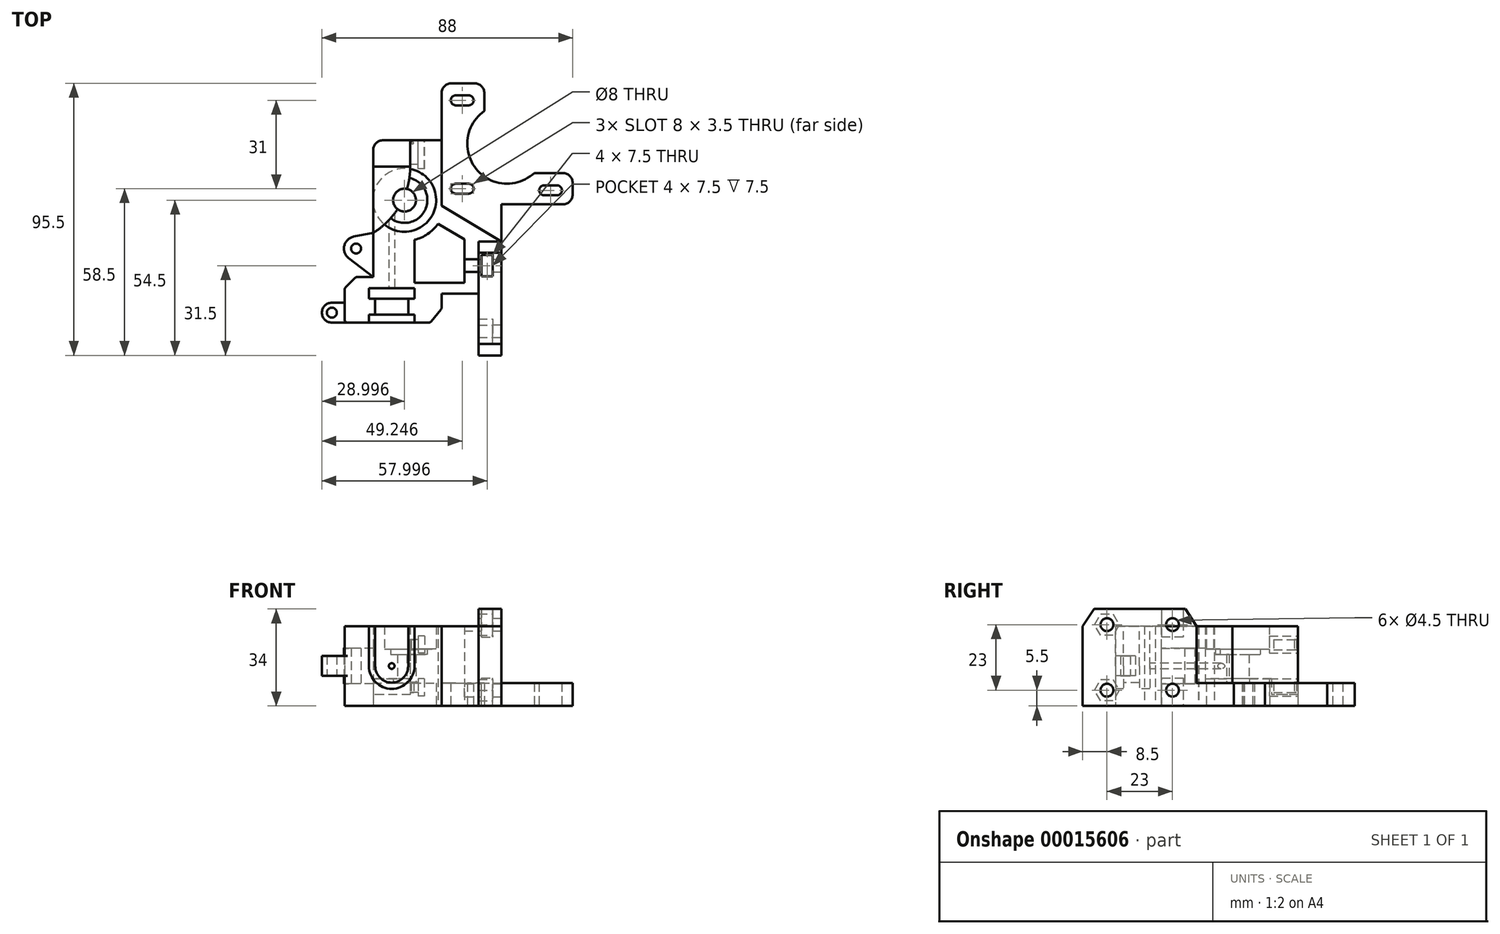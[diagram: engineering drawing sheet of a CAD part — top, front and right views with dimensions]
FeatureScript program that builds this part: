
annotation { "Feature Type Name" : "Feature", "Feature Type Description" : "" }
export const myFeature = defineFeature(function(context is Context, id is Id, definition is map)
    precondition{}
    {
        {
            var Q0;
            Q0=qCreatedBy(makeId("Top.planeOp"),FACE);
            var sketch = newSketch(context, id + "F0", { "sketchPlane" : qUnion([Q0])});
            skLineSegment(sketch, "E0.left", {"start": v(8.19, 39) * mm, "end": v(8.19, 0) * mm});
            skLineSegment(sketch, "E1", {"start": v(13.19, 7.25) * mm, "end": v(17.69, 7.25) * mm});
            skArc(sketch, "E2", {"start": v(13.19, 7.25) * mm, "mid": v(11.44, 5.5) * mm, "end": v(13.19, 3.75) * mm});
            skLineSegment(sketch, "E3", {"start": v(17.69, 3.75) * mm, "end": v(13.19, 3.75) * mm});
            skArc(sketch, "E4", {"start": v(17.69, 3.75) * mm, "mid": v(19.44, 5.5) * mm, "end": v(17.69, 7.25) * mm});
            skLineSegment(sketch, "E5", {"start": v(11.69, 42.5) * mm, "end": v(19.69, 42.5) * mm});
            skLineSegment(sketch, "E6", {"start": v(23.19, 39) * mm, "end": v(23.19, 32.76) * mm});
            skLineSegment(sketch, "E7", {"start": v(54.19, 3.5) * mm, "end": v(54.19, 7.5) * mm});
            skLineSegment(sketch, "E8", {"start": v(50.69, 11) * mm, "end": v(40.7, 11) * mm});
            skArc(sketch, "E9", {"start": v(23.19, 32.76) * mm, "mid": v(20.28, 12.5) * mm, "end": v(40.7, 11) * mm});
            skPoint(sketch, "E10.visualSharp", {"position": v(8.19, 42.5) * mm});
            skArc(sketch, "E10.filletArc", {"start": v(11.69, 42.5) * mm, "mid": v(9.21, 41.47) * mm, "end": v(8.19, 39) * mm});
            skPoint(sketch, "E11.visualSharp", {"position": v(23.19, 42.5) * mm});
            skArc(sketch, "E11.filletArc", {"start": v(23.19, 39) * mm, "mid": v(22.16, 41.47) * mm, "end": v(19.69, 42.5) * mm});
            skPoint(sketch, "E12.visualSharp", {"position": v(54.19, 11) * mm});
            skArc(sketch, "E12.filletArc", {"start": v(54.19, 7.5) * mm, "mid": v(53.16, 9.97) * mm, "end": v(50.69, 11) * mm});
            skPoint(sketch, "E13.visualSharp", {"position": v(54.19, 0) * mm});
            skArc(sketch, "E13.filletArc", {"start": v(50.69, 0) * mm, "mid": v(53.16, 1.03) * mm, "end": v(54.19, 3.5) * mm});
            skLineSegment(sketch, "E14", {"start": v(13.19, 38.25) * mm, "end": v(17.69, 38.25) * mm});
            skArc(sketch, "E15", {"start": v(17.69, 34.75) * mm, "mid": v(19.44, 36.5) * mm, "end": v(17.69, 38.25) * mm});
            skLineSegment(sketch, "E16", {"start": v(17.69, 34.75) * mm, "end": v(13.19, 34.75) * mm});
            skArc(sketch, "E17", {"start": v(13.19, 38.25) * mm, "mid": v(11.44, 36.5) * mm, "end": v(13.19, 34.75) * mm});
            skLineSegment(sketch, "E18", {"start": v(48.69, 3.18) * mm, "end": v(44.19, 3.18) * mm});
            skArc(sketch, "E19", {"start": v(44.19, 6.68) * mm, "mid": v(42.44, 4.93) * mm, "end": v(44.19, 3.18) * mm});
            skLineSegment(sketch, "E20", {"start": v(44.19, 6.68) * mm, "end": v(48.69, 6.68) * mm});
            skArc(sketch, "E21", {"start": v(48.69, 3.18) * mm, "mid": v(50.44, 4.93) * mm, "end": v(48.69, 6.68) * mm});
            skPoint(sketch, "E22", {"position": v(15.44, 38.25) * mm});
            skLineSegment(sketch, "E23", {"start": v(8.19, 22.5) * mm, "end": v(-12.31, 22.5) * mm});
            skLineSegment(sketch, "E24", {"start": v(8.19, 22.5) * mm, "end": v(8.19, -0.5) * mm});
            skLineSegment(sketch, "E25", {"start": v(8.19, -0.5) * mm, "end": v(29.19, -13) * mm});
            skLineSegment(sketch, "E26", {"start": v(29.19, -13) * mm, "end": v(29.19, 0) * mm});
            skLineSegment(sketch, "E27", {"start": v(-2.81, 22.5) * mm, "end": v(-2.81, 13.28) * mm});
            skLineSegment(sketch, "E28", {"start": v(50.69, 0) * mm, "end": v(29.19, 0) * mm});
            skLineSegment(sketch, "E29", {"start": v(-15.81, 19) * mm, "end": v(-15.81, -10) * mm});
            skLineSegment(sketch, "E30", {"start": v(-2.81, 13.28) * mm, "end": v(-15.81, 13.28) * mm});
            skCircle(sketch, "E31", {"center": v(-4.81, 1.5) * mm, "radius": 11.1 * mm});
            skCircle(sketch, "E32", {"center": v(-4.81, 1.5) * mm, "radius": 4 * mm});
            skCircle(sketch, "E33", {"center": v(-4.81, 1.5) * mm, "radius": 8 * mm});
            skLineSegment(sketch, "E34", {"start": v(29.19, -13) * mm, "end": v(29.19, -53) * mm});
            skLineSegment(sketch, "E35", {"start": v(29.19, -53) * mm, "end": v(21.19, -53) * mm});
            skLineSegment(sketch, "E36", {"start": v(21.19, -53) * mm, "end": v(21.19, -13) * mm});
            skLineSegment(sketch, "E37", {"start": v(21.19, -13) * mm, "end": v(29.19, -13) * mm});
            skLineSegment(sketch, "E38", {"start": v(-15.81, -10) * mm, "end": v(-15.81, -25.5) * mm});
            skLineSegment(sketch, "E39", {"start": v(-15.81, -25.5) * mm, "end": v(-21.81, -25.5) * mm});
            skLineSegment(sketch, "E40", {"start": v(-21.81, -25.5) * mm, "end": v(-25.81, -29.5) * mm});
            skLineSegment(sketch, "E41", {"start": v(-25.81, -29.5) * mm, "end": v(-25.81, -41.5) * mm});
            skLineSegment(sketch, "E42", {"start": v(-25.81, -41.5) * mm, "end": v(4.19, -41.5) * mm});
            skLineSegment(sketch, "E43", {"start": v(4.19, -41.5) * mm, "end": v(8.19, -36.59) * mm});
            skLineSegment(sketch, "E44", {"start": v(8.19, -36.59) * mm, "end": v(8.19, -31.28) * mm});
            skLineSegment(sketch, "E45", {"start": v(8.19, -31.28) * mm, "end": v(21.19, -31.28) * mm});
            skPoint(sketch, "E46", {"position": v(-21.81, -15.5) * mm});
            skPoint(sketch, "E47", {"position": v(-30.31, -38) * mm});
            skCircle(sketch, "E48", {"center": v(-30.31, -38) * mm, "radius": 1.75 * mm});
            skCircle(sketch, "E49", {"center": v(-21.81, -15.5) * mm, "radius": 1.75 * mm});
            skLineSegment(sketch, "E50", {"start": v(-25.81, -41.5) * mm, "end": v(-30.31, -41.5) * mm});
            skLineSegment(sketch, "E51", {"start": v(-25.81, -34.5) * mm, "end": v(-30.31, -34.5) * mm});
            skArc(sketch, "E52", {"start": v(-30.31, -34.5) * mm, "mid": v(-33.81, -38) * mm, "end": v(-30.31, -41.5) * mm});
            skLineSegment(sketch, "E53", {"start": v(-15.81, -25.5) * mm, "end": v(-24.41, -18.88) * mm});
            skLineSegment(sketch, "E54", {"start": v(-15.81, -10) * mm, "end": v(-22.62, -11.32) * mm});
            skArc(sketch, "E55", {"start": v(-22.62, -11.32) * mm, "mid": v(-25.96, -14.52) * mm, "end": v(-24.41, -18.88) * mm});
            skPoint(sketch, "E56.visualSharp", {"position": v(-15.81, 22.5) * mm});
            skArc(sketch, "E56.filletArc", {"start": v(-12.31, 22.5) * mm, "mid": v(-14.79, 21.47) * mm, "end": v(-15.81, 19) * mm});
            skLineSegment(sketch, "E57", {"start": v(-1.31, -12.45) * mm, "end": v(-1.31, -27.5) * mm});
            skLineSegment(sketch, "E58", {"start": v(-1.31, -27.5) * mm, "end": v(16.19, -27.5) * mm});
            skLineSegment(sketch, "E59", {"start": v(16.19, -27.5) * mm, "end": v(16.19, -12.28) * mm});
            skLineSegment(sketch, "E60", {"start": v(16.19, -12.28) * mm, "end": v(6.95, -6.78) * mm});
            skArc(sketch, "E61", {"start": v(-1.31, -12.45) * mm, "mid": v(3.33, -10.36) * mm, "end": v(6.95, -6.78) * mm});
            skArc(sketch, "E62", {"start": v(-15.81, -10) * mm, "mid": v(-6.28, -0.05) * mm, "end": v(-2.81, 13.28) * mm});
            skSolve(sketch);
        }
        {
            var Q0;
            {var subQ3=sQuery(id+"F0.wireOp",EDGE,"E27");Q0=makeQuery(id+"F0.imprint","IMPRINT",FACE,{"disambiguationData":[TD([[makeQuery(id+"F0.imprint","IMPRINT",EDGE,{"derivedFrom":subQ3}),-1.0]])]});}
            extrude(context, id + "F1", {"entities" : qUnion([Q0]), "depth" : 4 * mm});
        }
        {
            var Q0;
            {var subQ3=sQuery(id+"F0.wireOp",EDGE,"E0.left");Q0=makeQuery(id+"F0.imprint","IMPRINT",FACE,{"disambiguationData":[TD([[makeQuery(id+"F0.imprint","IMPRINT",EDGE,{"derivedFrom":subQ3}),1.0]])]});}
            extrude(context, id + "F2", {"entities" : qUnion([Q0]), "depth" : 8 * mm});
        }
        {
            var Q0;
            {var subQ3=sQuery(id+"F0.wireOp",EDGE,"E30");Q0=makeQuery(id+"F0.imprint","IMPRINT",FACE,{"disambiguationData":[TD([[makeQuery(id+"F0.imprint","IMPRINT",EDGE,{"derivedFrom":subQ3}),1.0]])]});}
            var Q1;
            {var subQ1=sQuery(id+"F0.wireOp",EDGE,"E31");var subQ3=sQuery(id+"F0.wireOp",EDGE,"E29");var subQ5=makeQuery(id+"F0.imprint","INTERSECT",VERTEX,{"derivedFrom":[subQ3,subQ1]});Q1=makeQuery(id+"F0.imprint","IMPRINT",FACE,{"disambiguationData":[TD([[makeQuery(id+"F0.imprint","IMPRINT",EDGE,{"disambiguationData":[TD([[subQ5,-1.0]])],"derivedFrom":subQ1}),-1.0]])]});}
            extrude(context, id + "F3", {"entities" : qUnion([Q0, Q1]), "operationType" : NewBodyOperationType.ADD, "depth" : 9.5 * mm});
        }
        {
            var Q0;
            {var subQ6=sQuery(id+"F0.wireOp",EDGE,"E25");Q0=makeQuery(id+"F0.imprint","IMPRINT",FACE,{"disambiguationData":[TD([[makeQuery(id+"F0.imprint","IMPRINT",EDGE,{"derivedFrom":subQ6}),-1.0]])]});}
            extrude(context, id + "F4", {"entities" : qUnion([Q0]), "depth" : 28 * mm});
        }
        {
            var Q0;
            {var subQ0=sQuery(id+"F0.wireOp",EDGE,"E62");var subQ3=sQuery(id+"F0.wireOp",EDGE,"E31");var subQ4=makeQuery(id+"F0.imprint","INTERSECT",VERTEX,{"disambiguationData":[OD(0.0)],"derivedFrom":[subQ3,subQ0]});Q0=makeQuery(id+"F0.imprint","IMPRINT",FACE,{"disambiguationData":[TD([[makeQuery(id+"F0.imprint","IMPRINT",EDGE,{"disambiguationData":[TD([[subQ4,1.0]])],"derivedFrom":subQ3}),1.0]])]});}
            var Q1;
            {var subQ0=sQuery(id+"F0.wireOp",EDGE,"E62");var subQ3=sQuery(id+"F0.wireOp",EDGE,"E32");var subQ6=makeQuery(id+"F0.imprint","INTERSECT",VERTEX,{"disambiguationData":[OD(0.0)],"derivedFrom":[subQ3,subQ0]});Q1=makeQuery(id+"F0.imprint","IMPRINT",FACE,{"disambiguationData":[TD([[makeQuery(id+"F0.imprint","IMPRINT",EDGE,{"disambiguationData":[TD([[subQ6,1.0]])],"derivedFrom":subQ3}),-1.0]])]});}
            var Q2;
            {var subQ0=sQuery(id+"F0.wireOp",EDGE,"E62");var subQ3=sQuery(id+"F0.wireOp",EDGE,"E32");var subQ6=makeQuery(id+"F0.imprint","INTERSECT",VERTEX,{"disambiguationData":[OD(0.0)],"derivedFrom":[subQ3,subQ0]});Q2=makeQuery(id+"F0.imprint","IMPRINT",FACE,{"disambiguationData":[TD([[makeQuery(id+"F0.imprint","IMPRINT",EDGE,{"disambiguationData":[TD([[subQ6,-1.0]])],"derivedFrom":subQ3}),-1.0]])]});}
            extrude(context, id + "F5", {"entities" : qUnion([Q0, Q1, Q2]), "depth" : 9.5 * mm, "hasSecondDirection" : true, "secondDirectionOppositeDirection" : false, "secondDirectionDepth" : 8 * mm});
        }
        {
            var Q0;
            {var subQ0=sQuery(id+"F0.wireOp",EDGE,"E62");var subQ3=sQuery(id+"F0.wireOp",EDGE,"E32");var subQ6=makeQuery(id+"F0.imprint","INTERSECT",VERTEX,{"disambiguationData":[OD(0.0)],"derivedFrom":[subQ3,subQ0]});Q0=makeQuery(id+"F0.imprint","IMPRINT",FACE,{"disambiguationData":[TD([[makeQuery(id+"F0.imprint","IMPRINT",EDGE,{"disambiguationData":[TD([[subQ6,-1.0]])],"derivedFrom":subQ3}),-1.0]])]});}
            extrude(context, id + "F6", {"entities" : qUnion([Q0]), "depth" : 18 * mm, "hasSecondDirection" : true, "secondDirectionOppositeDirection" : false, "secondDirectionDepth" : 8 * mm});
        }
        {
            var Q0;
            {var subQ0=sQuery(id+"F0.wireOp",EDGE,"E62");var subQ3=sQuery(id+"F0.wireOp",EDGE,"E31");var subQ6=makeQuery(id+"F0.imprint","INTERSECT",VERTEX,{"disambiguationData":[OD(0.0)],"derivedFrom":[subQ3,subQ0]});Q0=makeQuery(id+"F0.imprint","IMPRINT",FACE,{"disambiguationData":[TD([[makeQuery(id+"F0.imprint","IMPRINT",EDGE,{"disambiguationData":[TD([[subQ6,-1.0]])],"derivedFrom":subQ3}),1.0]])]});}
            extrude(context, id + "F7", {"entities" : qUnion([Q0]), "depth" : 9.5 * mm, "hasSecondDirection" : true, "secondDirectionOppositeDirection" : false, "secondDirectionDepth" : 8 * mm});
        }
        {
            var Q0;
            Q0=makeQuery(id+"F0.imprint","IMPRINT",FACE,{"disambiguationData":[TD([[makeQuery(id+"F0.imprint","IMPRINT",EDGE,{"derivedFrom":sQuery(id+"F0.wireOp",EDGE,"E48")}),-1.0]])]});
            extrude(context, id + "F8", {"entities" : qUnion([Q0]), "operationType" : NewBodyOperationType.ADD, "depth" : 17.5 * mm, "hasSecondDirection" : true, "secondDirectionOppositeDirection" : false, "secondDirectionDepth" : 10.5 * mm});
        }
        {
            var Q0;
            Q0=makeQuery(id+"F0.imprint","IMPRINT",FACE,{"disambiguationData":[TD([[makeQuery(id+"F0.imprint","IMPRINT",EDGE,{"derivedFrom":sQuery(id+"F0.wireOp",EDGE,"E38")}),-1.0]])]});
            extrude(context, id + "F9", {"entities" : qUnion([Q0]), "operationType" : NewBodyOperationType.ADD, "depth" : 20.25 * mm, "hasSecondDirection" : true, "secondDirectionOppositeDirection" : false, "secondDirectionDepth" : 7.75 * mm});
        }
        {
            var Q0;
            Q0=makeQuery(id+"F0.imprint","IMPRINT",FACE,{"disambiguationData":[TD([[makeQuery(id+"F0.imprint","IMPRINT",EDGE,{"derivedFrom":sQuery(id+"F0.wireOp",EDGE,"E34")}),-1.0]])]});
            extrude(context, id + "F10", {"entities" : qUnion([Q0]), "operationType" : NewBodyOperationType.ADD, "depth" : 34 * mm});
        }
        {
            var Q0;
            Q0=makeQuery(id+"F10.opExtrude","SWEPT_FACE",FACE,{"disambiguationData":[OSD([sQuery(id+"F0.wireOp",EDGE,"E34")])]});
            var sketch = newSketch(context, id + "F11", { "sketchPlane" : qUnion([Q0])});
            skLineSegment(sketch, "E63", {"start": v(-53, 28) * mm, "end": v(-49, 34) * mm});
            skLineSegment(sketch, "E64", {"start": v(-49, 34) * mm, "end": v(-17, 34) * mm});
            skLineSegment(sketch, "E65", {"start": v(-17, 34) * mm, "end": v(-13, 28) * mm});
            skLineSegment(sketch, "E66", {"start": v(-13, 28) * mm, "end": v(-13, 0) * mm});
            skLineSegment(sketch, "E67", {"start": v(-13, 0) * mm, "end": v(-53, 0) * mm});
            skLineSegment(sketch, "E68", {"start": v(-53, 0) * mm, "end": v(-53, 28) * mm});
            skPoint(sketch, "E69", {"position": v(-33, 34) * mm});
            skPoint(sketch, "E70", {"position": v(-53, 17) * mm});
            skPoint(sketch, "E71", {"position": v(-44.5, 28.5) * mm});
            skPoint(sketch, "E72", {"position": v(-21.5, 28.5) * mm});
            skPoint(sketch, "E73", {"position": v(-44.5, 5.5) * mm});
            skPoint(sketch, "E74", {"position": v(-21.5, 5.5) * mm});
            skCircle(sketch, "E75", {"center": v(-44.5, 28.5) * mm, "radius": 2.25 * mm});
            skCircle(sketch, "E76", {"center": v(-21.5, 28.5) * mm, "radius": 2.25 * mm});
            skCircle(sketch, "E77", {"center": v(-21.5, 5.5) * mm, "radius": 2.25 * mm});
            skCircle(sketch, "E78", {"center": v(-44.5, 5.5) * mm, "radius": 2.25 * mm});
            skPoint(sketch, "E79", {"position": v(-44.5, 32.25) * mm});
            skPoint(sketch, "E80", {"position": v(-44.5, 24.75) * mm});
            skCircle(sketch, "E81.cCircle", {"center": v(-44.5, 28.5) * mm, "radius": 3.75 * mm, "construction": true});
            skLineSegment(sketch, "E81.0", {"start": v(-46.67, 32.25) * mm, "end": v(-42.33, 32.25) * mm});
            skLineSegment(sketch, "E81.1", {"start": v(-42.33, 32.25) * mm, "end": v(-40.17, 28.5) * mm});
            skLineSegment(sketch, "E81.2", {"start": v(-40.17, 28.5) * mm, "end": v(-42.33, 24.75) * mm});
            skLineSegment(sketch, "E81.3", {"start": v(-42.33, 24.75) * mm, "end": v(-46.67, 24.75) * mm});
            skLineSegment(sketch, "E81.4", {"start": v(-46.67, 24.75) * mm, "end": v(-48.83, 28.5) * mm});
            skLineSegment(sketch, "E81.5", {"start": v(-48.83, 28.5) * mm, "end": v(-46.67, 32.25) * mm});
            skPoint(sketch, "E82", {"position": v(-21.5, 32.25) * mm});
            skPoint(sketch, "E83", {"position": v(-44.5, 1.75) * mm});
            skPoint(sketch, "E84", {"position": v(-21.5, 1.75) * mm});
            skCircle(sketch, "E85.cCircle", {"center": v(-44.5, 5.5) * mm, "radius": 3.75 * mm, "construction": true});
            skLineSegment(sketch, "E85.0", {"start": v(-42.33, 1.75) * mm, "end": v(-46.67, 1.75) * mm});
            skLineSegment(sketch, "E85.1", {"start": v(-46.67, 1.75) * mm, "end": v(-48.83, 5.5) * mm});
            skLineSegment(sketch, "E85.2", {"start": v(-48.83, 5.5) * mm, "end": v(-46.67, 9.25) * mm});
            skLineSegment(sketch, "E85.3", {"start": v(-46.67, 9.25) * mm, "end": v(-42.33, 9.25) * mm});
            skLineSegment(sketch, "E85.4", {"start": v(-42.33, 9.25) * mm, "end": v(-40.17, 5.5) * mm});
            skLineSegment(sketch, "E85.5", {"start": v(-40.17, 5.5) * mm, "end": v(-42.33, 1.75) * mm});
            skLineSegment(sketch, "E86", {"start": v(-17.75, 31.67) * mm, "end": v(-17.75, 24.17) * mm});
            skLineSegment(sketch, "E87", {"start": v(-17.75, 24.17) * mm, "end": v(-25.25, 24.17) * mm});
            skLineSegment(sketch, "E88", {"start": v(-25.25, 24.17) * mm, "end": v(-25.25, 31.67) * mm});
            skLineSegment(sketch, "E89", {"start": v(-17.75, 31.67) * mm, "end": v(-17.75, 34) * mm});
            skLineSegment(sketch, "E90", {"start": v(-17.75, 34) * mm, "end": v(-25.27, 34) * mm});
            skLineSegment(sketch, "E91.bottom", {"start": v(-25.25, 0) * mm, "end": v(-17.75, 0) * mm});
            skLineSegment(sketch, "E91.top", {"start": v(-25.25, 9.83) * mm, "end": v(-17.75, 9.83) * mm});
            skLineSegment(sketch, "E91.left", {"start": v(-25.25, 0) * mm, "end": v(-25.25, 9.83) * mm});
            skPoint(sketch, "E92.0.midPoint", {"position": v(-17.75, 5.5) * mm});
            skLineSegment(sketch, "E93", {"start": v(-17.75, 9.83) * mm, "end": v(-17.75, 0) * mm});
            skLineSegment(sketch, "E94", {"start": v(-25.25, 31.67) * mm, "end": v(-25.27, 34) * mm});
            skSolve(sketch);
        }
        {
            var Q0;
            {var subQ2=sQuery(id+"F11.wireOp",EDGE,"E63");Q0=makeQuery(id+"F11.imprint","IMPRINT",FACE,{"disambiguationData":[TD([[makeQuery(id+"F11.imprint","IMPRINT",EDGE,{"derivedFrom":subQ2}),1.0]])]});}
            extrude(context, id + "F12", {"entities" : qUnion([Q0]), "operationType" : NewBodyOperationType.REMOVE, "oppositeDirection" : true, "depth" : 9.03 * mm});
        }
        {
            var Q0;
            {var subQ2=sQuery(id+"F11.wireOp",EDGE,"E65");Q0=makeQuery(id+"F11.imprint","IMPRINT",FACE,{"disambiguationData":[TD([[makeQuery(id+"F11.imprint","IMPRINT",EDGE,{"derivedFrom":subQ2}),1.0]])]});}
            extrude(context, id + "F13", {"entities" : qUnion([Q0]), "operationType" : NewBodyOperationType.REMOVE, "oppositeDirection" : true, "depth" : 9 * mm});
        }
        {
            var Q0;
            Q0=makeQuery(id+"F8.boolean.opBoolean","MERGE",FACE,{"derivedFrom":[makeQuery(id+"F4.opExtrude","SWEPT_FACE",FACE,{"disambiguationData":[OSD([sQuery(id+"F0.wireOp",EDGE,"E42")])]}),makeQuery(id+"F8.opExtrude","SWEPT_FACE",FACE,{"disambiguationData":[OSD([sQuery(id+"F0.wireOp",EDGE,"E50")])]})]});
            var sketch = newSketch(context, id + "F14", { "sketchPlane" : qUnion([Q0])});
            skPoint(sketch, "E95", {"position": v(-9.31, 14) * mm});
            skPoint(sketch, "E96", {"position": v(4.19, 14) * mm});
            skPoint(sketch, "E97", {"position": v(-30.31, 14) * mm});
            skCircle(sketch, "E98", {"center": v(-9.31, 14) * mm, "radius": 1 * mm});
            skArc(sketch, "E99", {"start": v(-17.31, 14) * mm, "mid": v(-9.31, 6) * mm, "end": v(-1.31, 14) * mm});
            skLineSegment(sketch, "E100", {"start": v(-17.31, 14) * mm, "end": v(-17.31, 28) * mm});
            skLineSegment(sketch, "E101", {"start": v(-1.31, 14) * mm, "end": v(-1.31, 28) * mm});
            skLineSegment(sketch, "E102", {"start": v(-1.31, 28) * mm, "end": v(-17.31, 28) * mm});
            skArc(sketch, "E103", {"start": v(-15.11, 14) * mm, "mid": v(-9.31, 8.2) * mm, "end": v(-3.51, 14) * mm});
            skLineSegment(sketch, "E104", {"start": v(-15.11, 14) * mm, "end": v(-15.11, 28) * mm});
            skLineSegment(sketch, "E105", {"start": v(-3.51, 14) * mm, "end": v(-3.51, 28) * mm});
            skLineSegment(sketch, "E106", {"start": v(-3.51, 28) * mm, "end": v(-15.11, 28) * mm});
            skSolve(sketch);
        }
        {
            var Q0;
            Q0=makeQuery(id+"F11.imprint","IMPRINT",FACE,{"disambiguationData":[TD([[makeQuery(id+"F11.imprint","IMPRINT",EDGE,{"derivedFrom":sQuery(id+"F11.wireOp",EDGE,"E75")}),1.0]])]});
            var Q1;
            Q1=makeQuery(id+"F11.imprint","IMPRINT",FACE,{"disambiguationData":[TD([[makeQuery(id+"F11.imprint","IMPRINT",EDGE,{"derivedFrom":sQuery(id+"F11.wireOp",EDGE,"E78")}),1.0]])]});
            var Q2;
            Q2=makeQuery(id+"F11.imprint","IMPRINT",FACE,{"disambiguationData":[TD([[makeQuery(id+"F11.imprint","IMPRINT",EDGE,{"derivedFrom":sQuery(id+"F11.wireOp",EDGE,"E76")}),1.0]])]});
            var Q3;
            Q3=makeQuery(id+"F11.imprint","IMPRINT",FACE,{"disambiguationData":[TD([[makeQuery(id+"F11.imprint","IMPRINT",EDGE,{"derivedFrom":sQuery(id+"F11.wireOp",EDGE,"E77")}),1.0]])]});
            extrude(context, id + "F15", {"entities" : qUnion([Q0, Q1, Q2, Q3]), "operationType" : NewBodyOperationType.REMOVE, "oppositeDirection" : true, "depth" : 13 * mm});
        }
        {
            var Q0;
            Q0=makeQuery(id+"F11.imprint","IMPRINT",FACE,{"disambiguationData":[TD([[makeQuery(id+"F11.imprint","IMPRINT",EDGE,{"derivedFrom":sQuery(id+"F11.wireOp",EDGE,"E78")}),-1.0]])]});
            var Q1;
            Q1=makeQuery(id+"F11.imprint","IMPRINT",FACE,{"disambiguationData":[TD([[makeQuery(id+"F11.imprint","IMPRINT",EDGE,{"derivedFrom":sQuery(id+"F11.wireOp",EDGE,"E75")}),-1.0]])]});
            extrude(context, id + "F16", {"entities" : qUnion([Q0, Q1]), "operationType" : NewBodyOperationType.REMOVE, "oppositeDirection" : true, "depth" : 8 * mm, "hasSecondDirection" : true, "secondDirectionOppositeDirection" : true, "secondDirectionDepth" : 3 * mm});
        }
        {
            var Q0;
            Q0=makeQuery(id+"F11.imprint","IMPRINT",FACE,{"disambiguationData":[TD([[makeQuery(id+"F11.imprint","IMPRINT",EDGE,{"derivedFrom":sQuery(id+"F11.wireOp",EDGE,"E76")}),-1.0]])]});
            var Q1;
            Q1=makeQuery(id+"F11.imprint","IMPRINT",FACE,{"disambiguationData":[TD([[makeQuery(id+"F11.imprint","IMPRINT",EDGE,{"derivedFrom":sQuery(id+"F11.wireOp",EDGE,"E77")}),-1.0]])]});
            extrude(context, id + "F17", {"entities" : qUnion([Q0, Q1]), "operationType" : NewBodyOperationType.REMOVE, "oppositeDirection" : true, "depth" : 7 * mm, "hasSecondDirection" : true, "secondDirectionOppositeDirection" : true, "secondDirectionDepth" : 3 * mm});
        }
        {
            var Q0;
            Q0=makeQuery(id+"F14.imprint","IMPRINT",FACE,{"disambiguationData":[TD([[makeQuery(id+"F14.imprint","IMPRINT",EDGE,{"derivedFrom":sQuery(id+"F14.wireOp",EDGE,"E98")}),-1.0]])]});
            var Q1;
            Q1=makeQuery(id+"F14.imprint","IMPRINT",FACE,{"disambiguationData":[TD([[makeQuery(id+"F14.imprint","IMPRINT",EDGE,{"derivedFrom":sQuery(id+"F14.wireOp",EDGE,"E99")}),1.0]])]});
            extrude(context, id + "F18", {"entities" : qUnion([Q0, Q1]), "operationType" : NewBodyOperationType.REMOVE, "oppositeDirection" : true, "depth" : 12.1 * mm, "hasSecondDirection" : true, "secondDirectionOppositeDirection" : true, "secondDirectionDepth" : 8.35 * mm});
        }
        {
            var Q0;
            Q0=makeQuery(id+"F14.imprint","IMPRINT",FACE,{"disambiguationData":[TD([[makeQuery(id+"F14.imprint","IMPRINT",EDGE,{"derivedFrom":sQuery(id+"F14.wireOp",EDGE,"E98")}),1.0]])]});
            extrude(context, id + "F19", {"entities" : qUnion([Q0]), "operationType" : NewBodyOperationType.REMOVE, "oppositeDirection" : true, "depth" : 43.67 * mm});
        }
        {
            var Q0;
            Q0=makeQuery(id+"F14.imprint","IMPRINT",FACE,{"disambiguationData":[TD([[makeQuery(id+"F14.imprint","IMPRINT",EDGE,{"derivedFrom":sQuery(id+"F14.wireOp",EDGE,"E98")}),-1.0]])]});
            var Q1;
            Q1=makeQuery(id+"F14.imprint","IMPRINT",FACE,{"disambiguationData":[TD([[makeQuery(id+"F14.imprint","IMPRINT",EDGE,{"derivedFrom":sQuery(id+"F14.wireOp",EDGE,"E99")}),1.0]])]});
            extrude(context, id + "F20", {"entities" : qUnion([Q0, Q1]), "operationType" : NewBodyOperationType.REMOVE, "oppositeDirection" : true, "depth" : 2.75 * mm});
        }
        {
            var Q0;
            Q0=makeQuery(id+"F14.imprint","IMPRINT",FACE,{"disambiguationData":[TD([[makeQuery(id+"F14.imprint","IMPRINT",EDGE,{"derivedFrom":sQuery(id+"F14.wireOp",EDGE,"E98")}),-1.0]])]});
            extrude(context, id + "F21", {"entities" : qUnion([Q0]), "operationType" : NewBodyOperationType.REMOVE, "oppositeDirection" : true, "depth" : 9 * mm});
        }
        {
            var Q0;
            Q0=makeQuery(id+"F4.opExtrude","SWEPT_FACE",FACE,{"disambiguationData":[OSD([sQuery(id+"F0.wireOp",EDGE,"E23")])]});
            var sketch = newSketch(context, id + "F22", { "sketchPlane" : qUnion([Q0])});
            skLineSegment(sketch, "E107.bottom", {"start": v(-2.27, 24.5) * mm, "end": v(0, 24.5) * mm});
            skLineSegment(sketch, "E107.top", {"start": v(-2.27, 18.5) * mm, "end": v(0, 18.5) * mm});
            skLineSegment(sketch, "E107.left", {"start": v(-2.27, 24.5) * mm, "end": v(-2.27, 18.5) * mm});
            skLineSegment(sketch, "E107.right", {"start": v(0, 24.5) * mm, "end": v(0, 18.5) * mm});
            skLineSegment(sketch, "E108.bottom", {"start": v(-2.12, 9.5) * mm, "end": v(0, 9.5) * mm});
            skLineSegment(sketch, "E108.top", {"start": v(-2.12, 3.5) * mm, "end": v(0, 3.5) * mm});
            skLineSegment(sketch, "E108.left", {"start": v(-2.12, 9.5) * mm, "end": v(-2.12, 3.5) * mm});
            skLineSegment(sketch, "E108.right", {"start": v(0, 9.5) * mm, "end": v(0, 3.5) * mm});
            skPoint(sketch, "E109", {"position": v(0, 21.5) * mm});
            skPoint(sketch, "E110", {"position": v(0, 6.5) * mm});
            skLineSegment(sketch, "E111.bottom", {"start": v(0, 23.25) * mm, "end": v(2.81, 23.25) * mm});
            skLineSegment(sketch, "E111.top", {"start": v(0, 19.75) * mm, "end": v(2.81, 19.75) * mm});
            skLineSegment(sketch, "E111.left", {"start": v(0, 23.25) * mm, "end": v(0, 19.75) * mm});
            skLineSegment(sketch, "E111.right", {"start": v(2.81, 23.25) * mm, "end": v(2.81, 19.75) * mm});
            skLineSegment(sketch, "E112.bottom", {"start": v(0, 8.25) * mm, "end": v(2.81, 8.25) * mm});
            skLineSegment(sketch, "E112.top", {"start": v(0, 4.75) * mm, "end": v(2.81, 4.75) * mm});
            skLineSegment(sketch, "E112.left", {"start": v(0, 8.25) * mm, "end": v(0, 4.75) * mm});
            skLineSegment(sketch, "E112.right", {"start": v(2.81, 8.25) * mm, "end": v(2.81, 4.75) * mm});
            skSolve(sketch);
        }
        {
            var Q0;
            {var subQ3=sQuery(id+"F22.wireOp",EDGE,"E108.bottom");Q0=makeQuery(id+"F22.imprint","IMPRINT",FACE,{"disambiguationData":[TD([[makeQuery(id+"F22.imprint","IMPRINT",EDGE,{"derivedFrom":subQ3}),-1.0]])]});}
            var Q1;
            {var subQ3=sQuery(id+"F22.wireOp",EDGE,"E107.bottom");Q1=makeQuery(id+"F22.imprint","IMPRINT",FACE,{"disambiguationData":[TD([[makeQuery(id+"F22.imprint","IMPRINT",EDGE,{"derivedFrom":subQ3}),-1.0]])]});}
            extrude(context, id + "F23", {"entities" : qUnion([Q0, Q1]), "operationType" : NewBodyOperationType.REMOVE, "oppositeDirection" : true, "depth" : 10 * mm});
        }
        {
            var Q0;
            Q0=makeQuery(id+"F22.imprint","IMPRINT",FACE,{"disambiguationData":[TD([[makeQuery(id+"F22.imprint","IMPRINT",EDGE,{"derivedFrom":sQuery(id+"F22.wireOp",EDGE,"E112.bottom")}),-1.0]])]});
            var Q1;
            Q1=makeQuery(id+"F22.imprint","IMPRINT",FACE,{"disambiguationData":[TD([[makeQuery(id+"F22.imprint","IMPRINT",EDGE,{"derivedFrom":sQuery(id+"F22.wireOp",EDGE,"E111.bottom")}),-1.0]])]});
            extrude(context, id + "F24", {"entities" : qUnion([Q0, Q1]), "operationType" : NewBodyOperationType.REMOVE, "oppositeDirection" : true, "depth" : 8.5 * mm});
        }
        {
            var Q0;
            Q0=makeQuery(id+"F6.opExtrude","CAP_FACE",FACE,{"disambiguationData":[OSD([sQuery(id+"F0.wireOp",EDGE,"E32"),sQuery(id+"F0.wireOp",EDGE,"E33"),sQuery(id+"F0.wireOp",EDGE,"E62")])],"isStart":true});
            var sketch = newSketch(context, id + "F25", { "sketchPlane" : qUnion([Q0])});
            skLineSegment(sketch, "E113.bottom", {"start": v(-5.26, 9.03) * mm, "end": v(-5.04, 9.03) * mm});
            skLineSegment(sketch, "E113.top", {"start": v(-5.26, -12.01) * mm, "end": v(-5.04, -12.01) * mm});
            skLineSegment(sketch, "E113.left", {"start": v(-5.26, 9.03) * mm, "end": v(-5.26, -12.01) * mm});
            skLineSegment(sketch, "E113.right", {"start": v(-5.04, 9.03) * mm, "end": v(-5.04, -12.01) * mm});
            skLineSegment(sketch, "E114.bottom", {"start": v(-3.6, 8.67) * mm, "end": v(-3.34, 8.67) * mm});
            skLineSegment(sketch, "E114.top", {"start": v(-3.6, -12.01) * mm, "end": v(-3.34, -12.01) * mm});
            skLineSegment(sketch, "E114.left", {"start": v(-3.6, 8.67) * mm, "end": v(-3.6, -12.01) * mm});
            skLineSegment(sketch, "E114.right", {"start": v(-3.34, 8.67) * mm, "end": v(-3.34, -12.01) * mm});
            skLineSegment(sketch, "E115.bottom", {"start": v(-1.86, 7.95) * mm, "end": v(-1.6, 7.95) * mm});
            skLineSegment(sketch, "E115.top", {"start": v(-1.86, -11.22) * mm, "end": v(-1.6, -11.22) * mm});
            skLineSegment(sketch, "E115.left", {"start": v(-1.86, 7.95) * mm, "end": v(-1.86, -11.22) * mm});
            skLineSegment(sketch, "E115.right", {"start": v(-1.6, 7.95) * mm, "end": v(-1.6, -11.22) * mm});
            skLineSegment(sketch, "E116.bottom", {"start": v(-0.45, 7.08) * mm, "end": v(0, 7.08) * mm});
            skLineSegment(sketch, "E116.top", {"start": v(-0.45, -10.64) * mm, "end": v(0, -10.64) * mm});
            skLineSegment(sketch, "E116.left", {"start": v(-0.45, 7.08) * mm, "end": v(-0.45, -10.64) * mm});
            skLineSegment(sketch, "E116.right", {"start": v(0, 7.08) * mm, "end": v(0, -10.64) * mm});
            skLineSegment(sketch, "E117.bottom", {"start": v(1.4, 6.14) * mm, "end": v(1.61, 6.14) * mm});
            skLineSegment(sketch, "E117.top", {"start": v(1.4, -9.3) * mm, "end": v(1.61, -9.3) * mm});
            skLineSegment(sketch, "E117.left", {"start": v(1.4, 6.14) * mm, "end": v(1.4, -9.3) * mm});
            skLineSegment(sketch, "E117.right", {"start": v(1.61, 6.14) * mm, "end": v(1.61, -9.3) * mm});
            skLineSegment(sketch, "E118.bottom", {"start": v(3.5, 3.93) * mm, "end": v(3.75, 3.93) * mm});
            skLineSegment(sketch, "E118.top", {"start": v(3.5, -6.77) * mm, "end": v(3.75, -6.77) * mm});
            skLineSegment(sketch, "E118.left", {"start": v(3.5, 3.93) * mm, "end": v(3.5, -6.77) * mm});
            skLineSegment(sketch, "E118.right", {"start": v(3.75, 3.93) * mm, "end": v(3.75, -6.77) * mm});
            skLineSegment(sketch, "E119.bottom", {"start": v(-6.56, 8.42) * mm, "end": v(-6.78, 8.42) * mm});
            skLineSegment(sketch, "E119.top", {"start": v(-6.56, -11.36) * mm, "end": v(-6.78, -11.36) * mm});
            skLineSegment(sketch, "E119.left", {"start": v(-6.56, 8.42) * mm, "end": v(-6.56, -11.36) * mm});
            skLineSegment(sketch, "E119.right", {"start": v(-6.78, 8.42) * mm, "end": v(-6.78, -11.36) * mm});
            skLineSegment(sketch, "E120.bottom", {"start": v(-8.22, 7.48) * mm, "end": v(-8.48, 7.48) * mm});
            skLineSegment(sketch, "E120.top", {"start": v(-8.22, -10.71) * mm, "end": v(-8.48, -10.71) * mm});
            skLineSegment(sketch, "E120.left", {"start": v(-8.22, 7.48) * mm, "end": v(-8.22, -10.71) * mm});
            skLineSegment(sketch, "E120.right", {"start": v(-8.48, 7.48) * mm, "end": v(-8.48, -10.71) * mm});
            skLineSegment(sketch, "E121.bottom", {"start": v(-9.89, 6.28) * mm, "end": v(-10.14, 6.28) * mm});
            skLineSegment(sketch, "E121.top", {"start": v(-9.89, -9.84) * mm, "end": v(-10.14, -9.84) * mm});
            skLineSegment(sketch, "E121.left", {"start": v(-9.89, 6.28) * mm, "end": v(-9.89, -9.84) * mm});
            skLineSegment(sketch, "E121.right", {"start": v(-10.14, 6.28) * mm, "end": v(-10.14, -9.84) * mm});
            skLineSegment(sketch, "E122.bottom", {"start": v(-11.84, 4.8) * mm, "end": v(-12.13, 4.8) * mm});
            skLineSegment(sketch, "E122.top", {"start": v(-11.84, -8.76) * mm, "end": v(-12.13, -8.76) * mm});
            skLineSegment(sketch, "E122.left", {"start": v(-11.84, 4.8) * mm, "end": v(-11.84, -8.76) * mm});
            skLineSegment(sketch, "E122.right", {"start": v(-12.13, 4.8) * mm, "end": v(-12.13, -8.76) * mm});
            skLineSegment(sketch, "E123.bottom", {"start": v(-13.65, 1.26) * mm, "end": v(-13.86, 1.26) * mm});
            skLineSegment(sketch, "E123.top", {"start": v(-13.65, -4.89) * mm, "end": v(-13.86, -4.89) * mm});
            skLineSegment(sketch, "E123.left", {"start": v(-13.65, 1.26) * mm, "end": v(-13.65, -4.89) * mm});
            skLineSegment(sketch, "E123.right", {"start": v(-13.86, 1.26) * mm, "end": v(-13.86, -4.89) * mm});
            skSolve(sketch);
        }
        {
            var Q0;
            {var subQ0=sQuery(id+"F0.wireOp",EDGE,"E41");var subQ1=sQuery(id+"F0.wireOp",EDGE,"E42");var subQ2=sQuery(id+"F0.wireOp",EDGE,"E50");Q0=makeQuery(id+"F8.boolean.opBoolean","SPLIT",EDGE,{"disambiguationData":[TD([makeQuery(id+"F8.opExtrude","CAP_FACE",FACE,{"disambiguationData":[OSD([subQ0,sQuery(id+"F0.wireOp",EDGE,"E48"),subQ2,sQuery(id+"F0.wireOp",EDGE,"E51"),sQuery(id+"F0.wireOp",EDGE,"E52")])],"isStart":false})])],"derivedFrom":makeQuery(id+"F4.opExtrude","SWEPT_EDGE",EDGE,{"disambiguationData":[OSD([subQ0,subQ1,subQ2])]})});}
            var Q1;
            {var subQ0=sQuery(id+"F0.wireOp",EDGE,"E41");var subQ1=sQuery(id+"F0.wireOp",EDGE,"E42");var subQ2=sQuery(id+"F0.wireOp",EDGE,"E50");Q1=makeQuery(id+"F8.boolean.opBoolean","SPLIT",EDGE,{"disambiguationData":[TD([makeQuery(id+"F8.opExtrude","CAP_FACE",FACE,{"disambiguationData":[OSD([subQ0,sQuery(id+"F0.wireOp",EDGE,"E48"),subQ2,sQuery(id+"F0.wireOp",EDGE,"E51"),sQuery(id+"F0.wireOp",EDGE,"E52")])],"isStart":true})])],"derivedFrom":makeQuery(id+"F4.opExtrude","SWEPT_EDGE",EDGE,{"disambiguationData":[OSD([subQ0,subQ1,subQ2])]})});}
            var Q2;
            Q2=makeQuery(id+"F4.opExtrude","SWEPT_EDGE",EDGE,{"disambiguationData":[OSD([sQuery(id+"F0.wireOp",EDGE,"E40"),sQuery(id+"F0.wireOp",EDGE,"E41")])]});
            var Q3;
            Q3=makeQuery(id+"F4.opExtrude","SWEPT_EDGE",EDGE,{"disambiguationData":[OSD([sQuery(id+"F0.wireOp",EDGE,"E39"),sQuery(id+"F0.wireOp",EDGE,"E40")])]});
            var Q4;
            Q4=makeQuery(id+"F4.opExtrude","SWEPT_EDGE",EDGE,{"disambiguationData":[OSD([sQuery(id+"F0.wireOp",EDGE,"E42"),sQuery(id+"F0.wireOp",EDGE,"E43")])]});
            var Q5;
            Q5=makeQuery(id+"F4.opExtrude","SWEPT_EDGE",EDGE,{"disambiguationData":[OSD([sQuery(id+"F0.wireOp",EDGE,"E43"),sQuery(id+"F0.wireOp",EDGE,"E44")])]});
            var Q6;
            {var subQ0=sQuery(id+"F0.wireOp",EDGE,"E23");var subQ1=sQuery(id+"F0.wireOp",EDGE,"E27");Q6=makeQuery(id+"F24.boolean.opBoolean","SPLIT",EDGE,{"disambiguationData":[TD([makeQuery(id+"F24.opExtrude","SWEPT_FACE",FACE,{"disambiguationData":[OSD([sQuery(id+"F22.wireOp",EDGE,"E111.top")])]})])],"derivedFrom":makeQuery(id+"F4.opExtrude","SWEPT_EDGE",EDGE,{"disambiguationData":[OSD([subQ0,subQ1])]})});}
            var Q7;
            {var subQ0=sQuery(id+"F0.wireOp",EDGE,"E23");var subQ1=sQuery(id+"F0.wireOp",EDGE,"E27");Q7=makeQuery(id+"F24.boolean.opBoolean","SPLIT",EDGE,{"disambiguationData":[TD([makeQuery(id+"F24.opExtrude","SWEPT_FACE",FACE,{"disambiguationData":[OSD([sQuery(id+"F22.wireOp",EDGE,"E111.bottom")])]})])],"derivedFrom":makeQuery(id+"F4.opExtrude","SWEPT_EDGE",EDGE,{"disambiguationData":[OSD([subQ0,subQ1])]})});}
            fillet(context, id + "F26", {"entities" : qUnion([Q0, Q1, Q2, Q3, Q4, Q5, Q6, Q7]), "radius" : 1 * mm, "tangentPropagation" : true, "allowEdgeOverflow" : false});
        }
        {
            var Q0;
            Q0=makeQuery(id+"F9.opExtrude","CAP_FACE",FACE,{"disambiguationData":[OSD([sQuery(id+"F0.wireOp",EDGE,"E38"),sQuery(id+"F0.wireOp",EDGE,"E49"),sQuery(id+"F0.wireOp",EDGE,"E53"),sQuery(id+"F0.wireOp",EDGE,"E54"),sQuery(id+"F0.wireOp",EDGE,"E55")])],"isStart":true});
            var sketch = newSketch(context, id + "F27", { "sketchPlane" : qUnion([Q0])});
            skLineSegment(sketch, "E124.bottom", {"start": v(-17.02, 22.68) * mm, "end": v(-17.41, 22.68) * mm});
            skLineSegment(sketch, "E124.top", {"start": v(-17.02, 11.25) * mm, "end": v(-17.41, 11.25) * mm});
            skLineSegment(sketch, "E124.left", {"start": v(-17.02, 22.68) * mm, "end": v(-17.02, 11.25) * mm});
            skLineSegment(sketch, "E124.right", {"start": v(-17.41, 22.68) * mm, "end": v(-17.41, 11.25) * mm});
            skLineSegment(sketch, "E125.bottom", {"start": v(-18.94, 21.94) * mm, "end": v(-19.29, 21.94) * mm});
            skLineSegment(sketch, "E125.top", {"start": v(-18.94, 11.65) * mm, "end": v(-19.29, 11.65) * mm});
            skLineSegment(sketch, "E125.left", {"start": v(-18.94, 21.94) * mm, "end": v(-18.94, 11.65) * mm});
            skLineSegment(sketch, "E125.right", {"start": v(-19.29, 21.94) * mm, "end": v(-19.29, 11.65) * mm});
            skLineSegment(sketch, "E126.bottom", {"start": v(-23.18, 12.88) * mm, "end": v(-19.88, 12.88) * mm});
            skLineSegment(sketch, "E126.top", {"start": v(-23.18, 12.43) * mm, "end": v(-19.88, 12.43) * mm});
            skLineSegment(sketch, "E126.left", {"start": v(-23.18, 12.88) * mm, "end": v(-23.18, 12.43) * mm});
            skLineSegment(sketch, "E126.right", {"start": v(-19.88, 12.88) * mm, "end": v(-19.88, 12.43) * mm});
            skLineSegment(sketch, "E127.bottom", {"start": v(-23.18, 17.7) * mm, "end": v(-19.73, 17.7) * mm});
            skLineSegment(sketch, "E127.top", {"start": v(-23.18, 18) * mm, "end": v(-19.73, 18) * mm});
            skLineSegment(sketch, "E127.left", {"start": v(-23.18, 17.7) * mm, "end": v(-23.18, 18) * mm});
            skLineSegment(sketch, "E127.right", {"start": v(-19.73, 17.7) * mm, "end": v(-19.73, 18) * mm});
            skLineSegment(sketch, "E128.bottom", {"start": v(-21.75, 19.28) * mm, "end": v(-19.83, 19.28) * mm});
            skLineSegment(sketch, "E128.top", {"start": v(-21.75, 19.58) * mm, "end": v(-19.83, 19.58) * mm});
            skLineSegment(sketch, "E128.left", {"start": v(-21.75, 19.28) * mm, "end": v(-21.75, 19.58) * mm});
            skLineSegment(sketch, "E128.right", {"start": v(-19.83, 19.28) * mm, "end": v(-19.83, 19.58) * mm});
            skLineSegment(sketch, "E129.bottom", {"start": v(-23.92, 16.82) * mm, "end": v(-24.46, 16.82) * mm});
            skLineSegment(sketch, "E129.top", {"start": v(-23.92, 13.91) * mm, "end": v(-24.46, 13.91) * mm});
            skLineSegment(sketch, "E129.left", {"start": v(-23.92, 16.82) * mm, "end": v(-23.92, 13.91) * mm});
            skLineSegment(sketch, "E129.right", {"start": v(-24.46, 16.82) * mm, "end": v(-24.46, 13.91) * mm});
            skSolve(sketch);
        }
        {
            var Q0;
            Q0=makeQuery(id+"F0.imprint","IMPRINT",FACE,{"disambiguationData":[TD([[makeQuery(id+"F0.imprint","IMPRINT",EDGE,{"derivedFrom":sQuery(id+"F0.wireOp",EDGE,"E48")}),-1.0]])]});
            var sketch = newSketch(context, id + "F28", { "sketchPlane" : qUnion([Q0])});
            skLineSegment(sketch, "E130.bottom", {"start": v(-26.5, -40.74) * mm, "end": v(-26.92, -40.74) * mm});
            skLineSegment(sketch, "E130.top", {"start": v(-26.5, -35.03) * mm, "end": v(-26.92, -35.03) * mm});
            skLineSegment(sketch, "E130.left", {"start": v(-26.5, -40.74) * mm, "end": v(-26.5, -35.03) * mm});
            skLineSegment(sketch, "E130.right", {"start": v(-26.92, -40.74) * mm, "end": v(-26.92, -35.03) * mm});
            skLineSegment(sketch, "E131.bottom", {"start": v(-31.66, -40.04) * mm, "end": v(-27.76, -40.04) * mm});
            skLineSegment(sketch, "E131.top", {"start": v(-31.66, -40.74) * mm, "end": v(-27.76, -40.74) * mm});
            skLineSegment(sketch, "E131.left", {"start": v(-31.66, -40.04) * mm, "end": v(-31.66, -40.74) * mm});
            skLineSegment(sketch, "E131.right", {"start": v(-27.76, -40.04) * mm, "end": v(-27.76, -40.74) * mm});
            skLineSegment(sketch, "E132.bottom", {"start": v(-27.82, -36) * mm, "end": v(-31.73, -36) * mm});
            skLineSegment(sketch, "E132.top", {"start": v(-27.82, -35.58) * mm, "end": v(-31.73, -35.58) * mm});
            skLineSegment(sketch, "E132.left", {"start": v(-27.82, -36) * mm, "end": v(-27.82, -35.58) * mm});
            skLineSegment(sketch, "E132.right", {"start": v(-31.73, -36) * mm, "end": v(-31.73, -35.58) * mm});
            skLineSegment(sketch, "E133.bottom", {"start": v(-32.67, -39.63) * mm, "end": v(-32.21, -39.63) * mm});
            skLineSegment(sketch, "E133.top", {"start": v(-32.67, -36.35) * mm, "end": v(-32.21, -36.35) * mm});
            skLineSegment(sketch, "E133.left", {"start": v(-32.67, -39.63) * mm, "end": v(-32.67, -36.35) * mm});
            skLineSegment(sketch, "E133.right", {"start": v(-32.21, -39.63) * mm, "end": v(-32.21, -36.35) * mm});
            skLineSegment(sketch, "E134.bottom", {"start": v(-27.86, -39.2) * mm, "end": v(-27.44, -39.2) * mm});
            skLineSegment(sketch, "E134.top", {"start": v(-27.86, -36.7) * mm, "end": v(-27.44, -36.7) * mm});
            skLineSegment(sketch, "E134.left", {"start": v(-27.86, -39.2) * mm, "end": v(-27.86, -36.7) * mm});
            skLineSegment(sketch, "E134.right", {"start": v(-27.44, -39.2) * mm, "end": v(-27.44, -36.7) * mm});
            skSolve(sketch);
        }
        {
            var Q0;
            {var subQ0=sQuery(id+"F0.wireOp",EDGE,"E62");var subQ3=sQuery(id+"F0.wireOp",EDGE,"E31");var subQ4=makeQuery(id+"F0.imprint","INTERSECT",VERTEX,{"disambiguationData":[OD(0.0)],"derivedFrom":[subQ3,subQ0]});Q0=makeQuery(id+"F0.imprint","IMPRINT",FACE,{"disambiguationData":[TD([[makeQuery(id+"F0.imprint","IMPRINT",EDGE,{"disambiguationData":[TD([[subQ4,1.0]])],"derivedFrom":subQ3}),1.0]])]});}
            extrude(context, id + "F29", {"entities" : qUnion([Q0]), "operationType" : NewBodyOperationType.ADD, "depth" : 20 * mm, "hasSecondDirection" : true, "secondDirectionOppositeDirection" : false, "secondDirectionDepth" : 9 * mm});
        }
        {
            var Q0;
            Q0=makeQuery(id+"F14.imprint","IMPRINT",FACE,{"disambiguationData":[TD([[makeQuery(id+"F14.imprint","IMPRINT",EDGE,{"derivedFrom":sQuery(id+"F14.wireOp",EDGE,"E98")}),1.0]])]});
            extrude(context, id + "F30", {"entities" : qUnion([Q0]), "operationType" : NewBodyOperationType.REMOVE, "oppositeDirection" : true, "depth" : 44.4 * mm});
        }
        {
            var Q0;
            Q0=makeQuery(id+"F24.boolean.opBoolean","COPY",FACE,{"derivedFrom":makeQuery(id+"F24.opExtrude","SWEPT_FACE",FACE,{"disambiguationData":[OSD([sQuery(id+"F22.wireOp",EDGE,"E112.top")])]})});
            var sketch = newSketch(context, id + "F31", { "sketchPlane" : qUnion([Q0])});
            skCircle(sketch, "E135", {"center": v(-2, 21.59) * mm, "radius": 0.39 * mm});
            skSolve(sketch);
        }
        {
            var Q0;
            Q0=makeQuery(id+"F31.imprint","IMPRINT",FACE,{"disambiguationData":[TD([[makeQuery(id+"F31.imprint","IMPRINT",EDGE,{"derivedFrom":sQuery(id+"F31.wireOp",EDGE,"E135")}),1.0]])]});
            extrude(context, id + "F32", {"entities" : qUnion([Q0]), "operationType" : NewBodyOperationType.ADD, "depth" : 20.8 * mm});
        }
    });
